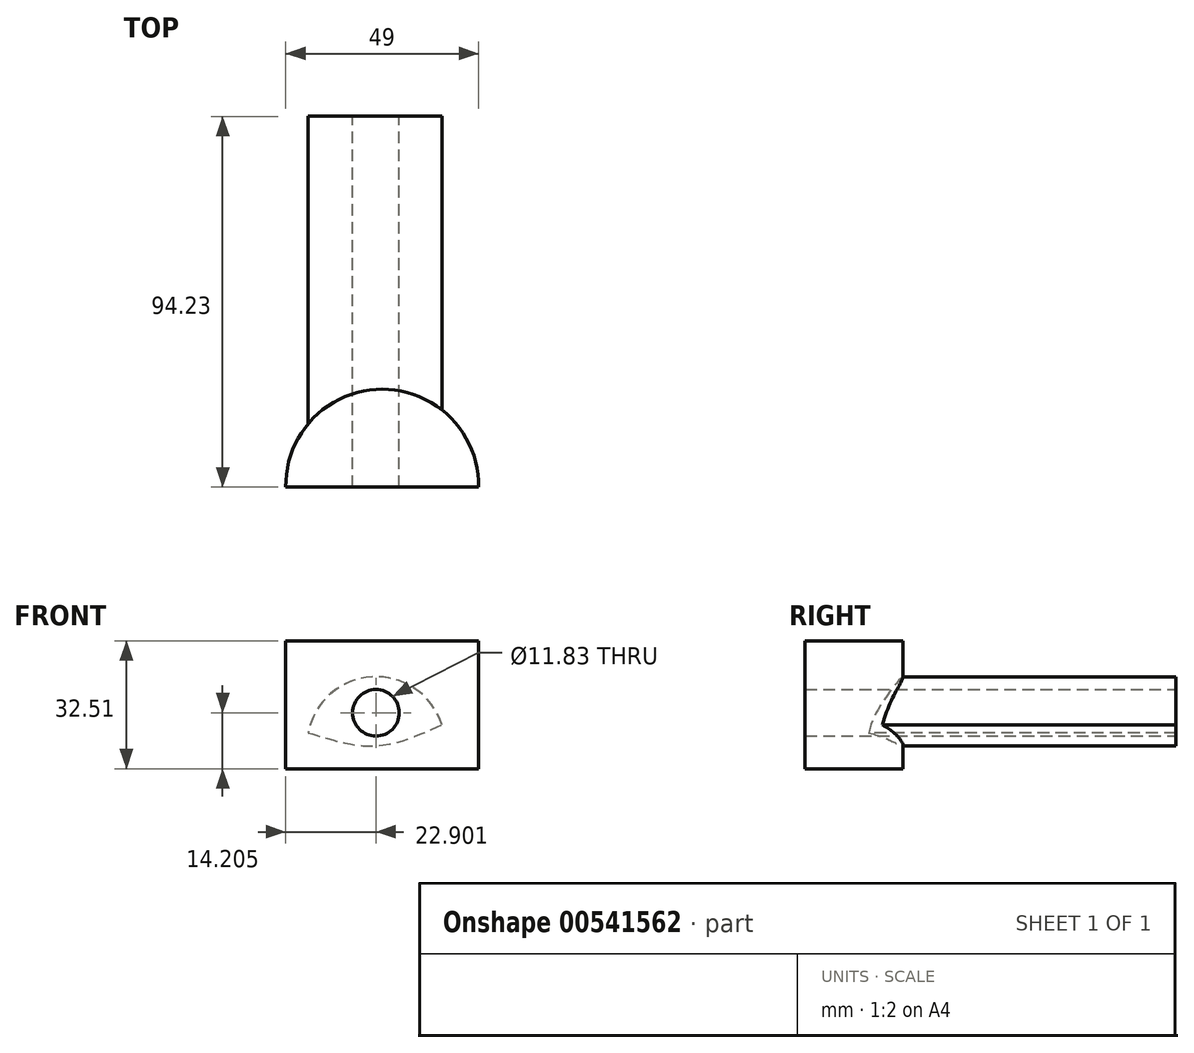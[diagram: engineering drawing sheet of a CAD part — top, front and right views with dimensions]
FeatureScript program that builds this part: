
annotation { "Feature Type Name" : "Feature", "Feature Type Description" : "" }
export const myFeature = defineFeature(function(context is Context, id is Id, definition is map)
    precondition{}
    {
        {
            var Q0;
            Q0=qCreatedBy(makeId("Top.planeOp"),FACE);
            var sketch = newSketch(context, id + "F0", { "sketchPlane" : qUnion([Q0])});
            skArc(sketch, "E0", {"start": v(49, 0) * mm, "mid": v(24.5, 24.91) * mm, "end": v(0, 0) * mm});
            skLineSegment(sketch, "E1", {"start": v(0, 0) * mm, "end": v(49, 0) * mm});
            skSolve(sketch);
        }
        {
            var Q0;
            Q0=makeQuery(id+"F0.imprint","IMPRINT",FACE,{"disambiguationData":[TD([[makeQuery(id+"F0.imprint","IMPRINT",EDGE,{"derivedFrom":sQuery(id+"F0.wireOp",EDGE,"E0")}),1.0]])]});
            extrude(context, id + "F1", {"entities" : qUnion([Q0]), "depth" : 32.5 * mm});
        }
        {
            var Q0;
            Q0=makeQuery(id+"F1.opExtrude","SWEPT_FACE",FACE,{"disambiguationData":[OSD([sQuery(id+"F0.wireOp",EDGE,"E1")])]});
            var sketch = newSketch(context, id + "F2", { "sketchPlane" : qUnion([Q0])});
            skArc(sketch, "E2", {"start": v(39.67, 11.17) * mm, "mid": v(21.9, 23.34) * mm, "end": v(5.7, 9.13) * mm});
            skFitSpline(sketch, "E3", {"points": [v(5.7, 9.13) * mm, v(22.95, 5.82) * mm, v(39.67, 11.17) * mm], "startDerivative": vector(34.75, -10.96) * mm, "endDerivative": vector(33.18, 15.05) * mm});
            skSolve(sketch);
        }
        {
            var Q0;
            Q0=makeQuery(id+"F2.imprint","IMPRINT",FACE,{"disambiguationData":[TD([[makeQuery(id+"F2.imprint","IMPRINT",EDGE,{"derivedFrom":sQuery(id+"F2.wireOp",EDGE,"E2")}),1.0]])]});
            extrude(context, id + "F3", {"entities" : qUnion([Q0]), "operationType" : NewBodyOperationType.ADD, "oppositeDirection" : true, "depth" : 45.72 * mm});
        }
        {
            var Q0;
            Q0=makeQuery(id+"F3.opExtrude","CAP_FACE",FACE,{"disambiguationData":[OSD([sQuery(id+"F2.wireOp",EDGE,"E2"),sQuery(id+"F2.wireOp",EDGE,"E3")])],"isStart":false});
            extrude(context, id + "F4", {"entities" : qUnion([Q0]), "operationType" : NewBodyOperationType.ADD, "depth" : 48.5 * mm});
        }
        {
            var Q0;
            Q0=makeQuery(id+"F4.opExtrude","CAP_FACE",FACE,{"disambiguationData":[OSD([sQuery(id+"F2.wireOp",EDGE,"E2"),sQuery(id+"F2.wireOp",EDGE,"E3")])],"isStart":false});
            var sketch = newSketch(context, id + "F5", { "sketchPlane" : qUnion([Q0])});
            skCircle(sketch, "E4", {"center": v(-22.9, 14.2) * mm, "radius": 5.91 * mm});
            skSolve(sketch);
        }
        {
            var Q0;
            Q0=qSketchRegion(id+"F5",true);
            extrude(context, id + "F6", {"entities" : qUnion([Q0]), "operationType" : NewBodyOperationType.REMOVE, "oppositeDirection" : true, "depth" : 140.2 * mm});
        }
    });
